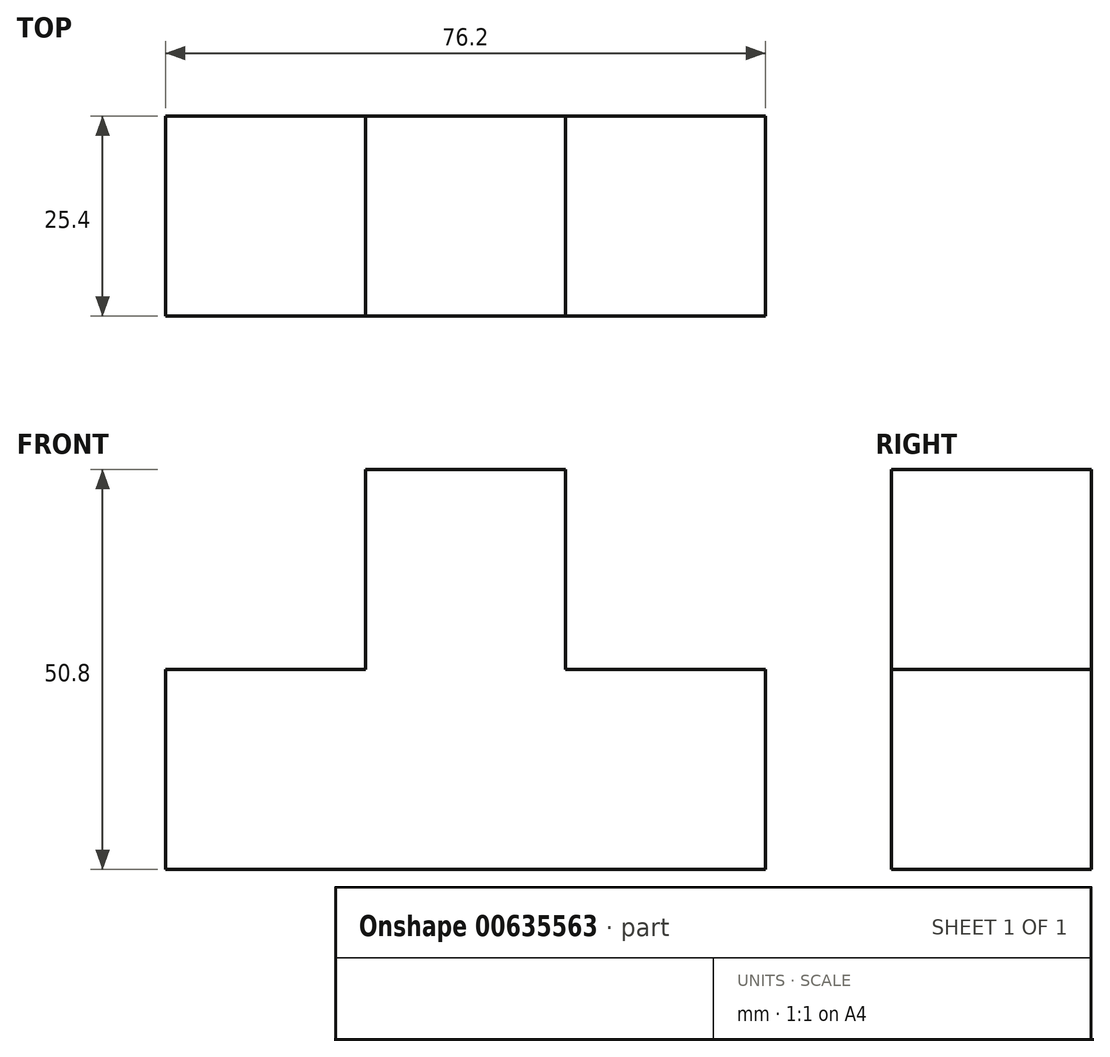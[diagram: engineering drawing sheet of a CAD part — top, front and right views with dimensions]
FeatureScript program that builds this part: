
annotation { "Feature Type Name" : "Feature", "Feature Type Description" : "" }
export const myFeature = defineFeature(function(context is Context, id is Id, definition is map)
    precondition{}
    {
        {
            var Q0;
            Q0=qCreatedBy(makeId("Top.planeOp"),FACE);
            var sketch = newSketch(context, id + "F0", { "sketchPlane" : qUnion([Q0])});
            skLineSegment(sketch, "E0.bottom", {"start": v(0, 0) * mm, "end": v(50.8, 0) * mm});
            skLineSegment(sketch, "E0.top", {"start": v(0, 25.4) * mm, "end": v(50.8, 25.4) * mm});
            skLineSegment(sketch, "E0.left", {"start": v(0, 0) * mm, "end": v(0, 25.4) * mm});
            skLineSegment(sketch, "E0.right", {"start": v(50.8, 0) * mm, "end": v(50.8, 25.4) * mm});
            skLineSegment(sketch, "E1.bottom", {"start": v(25.4, 0) * mm, "end": v(76.2, 0) * mm});
            skLineSegment(sketch, "E1.top", {"start": v(25.4, 25.4) * mm, "end": v(76.2, 25.4) * mm});
            skLineSegment(sketch, "E1.left", {"start": v(25.4, 0) * mm, "end": v(25.4, 25.4) * mm});
            skLineSegment(sketch, "E1.right", {"start": v(76.2, 0) * mm, "end": v(76.2, 25.4) * mm});
            skSolve(sketch);
        }
        {
            var Q0;
            Q0=makeQuery(id+"F0.imprint","IMPRINT",FACE,{"disambiguationData":[TD([[makeQuery(id+"F0.imprint","IMPRINT",EDGE,{"derivedFrom":sQuery(id+"F0.wireOp",EDGE,"E0.bottom")}),1.0]])]});
            var Q1;
            {var subQ0=sQuery(id+"F0.wireOp",EDGE,"E0.right");Q1=makeQuery(id+"F0.imprint","IMPRINT",FACE,{"disambiguationData":[TD([[makeQuery(id+"F0.imprint","IMPRINT",EDGE,{"derivedFrom":subQ0}),1.0]])]});}
            var Q2;
            {var subQ0=sQuery(id+"F0.wireOp",EDGE,"E0.right");Q2=makeQuery(id+"F0.imprint","IMPRINT",FACE,{"disambiguationData":[TD([[makeQuery(id+"F0.imprint","IMPRINT",EDGE,{"derivedFrom":subQ0}),-1.0]])]});}
            extrude(context, id + "F1", {"entities" : qUnion([Q0, Q1, Q2]), "depth" : 25.4 * mm, "offsetDistance" : 25.4 * mm});
        }
        {
            var Q0;
            {var subQ0=sQuery(id+"F0.wireOp",EDGE,"E0.right");Q0=makeQuery(id+"F0.imprint","IMPRINT",FACE,{"disambiguationData":[TD([[makeQuery(id+"F0.imprint","IMPRINT",EDGE,{"derivedFrom":subQ0}),1.0]])]});}
            extrude(context, id + "F2", {"entities" : qUnion([Q0]), "operationType" : NewBodyOperationType.ADD, "depth" : 50.8 * mm, "offsetDistance" : 25.4 * mm});
        }
    });
